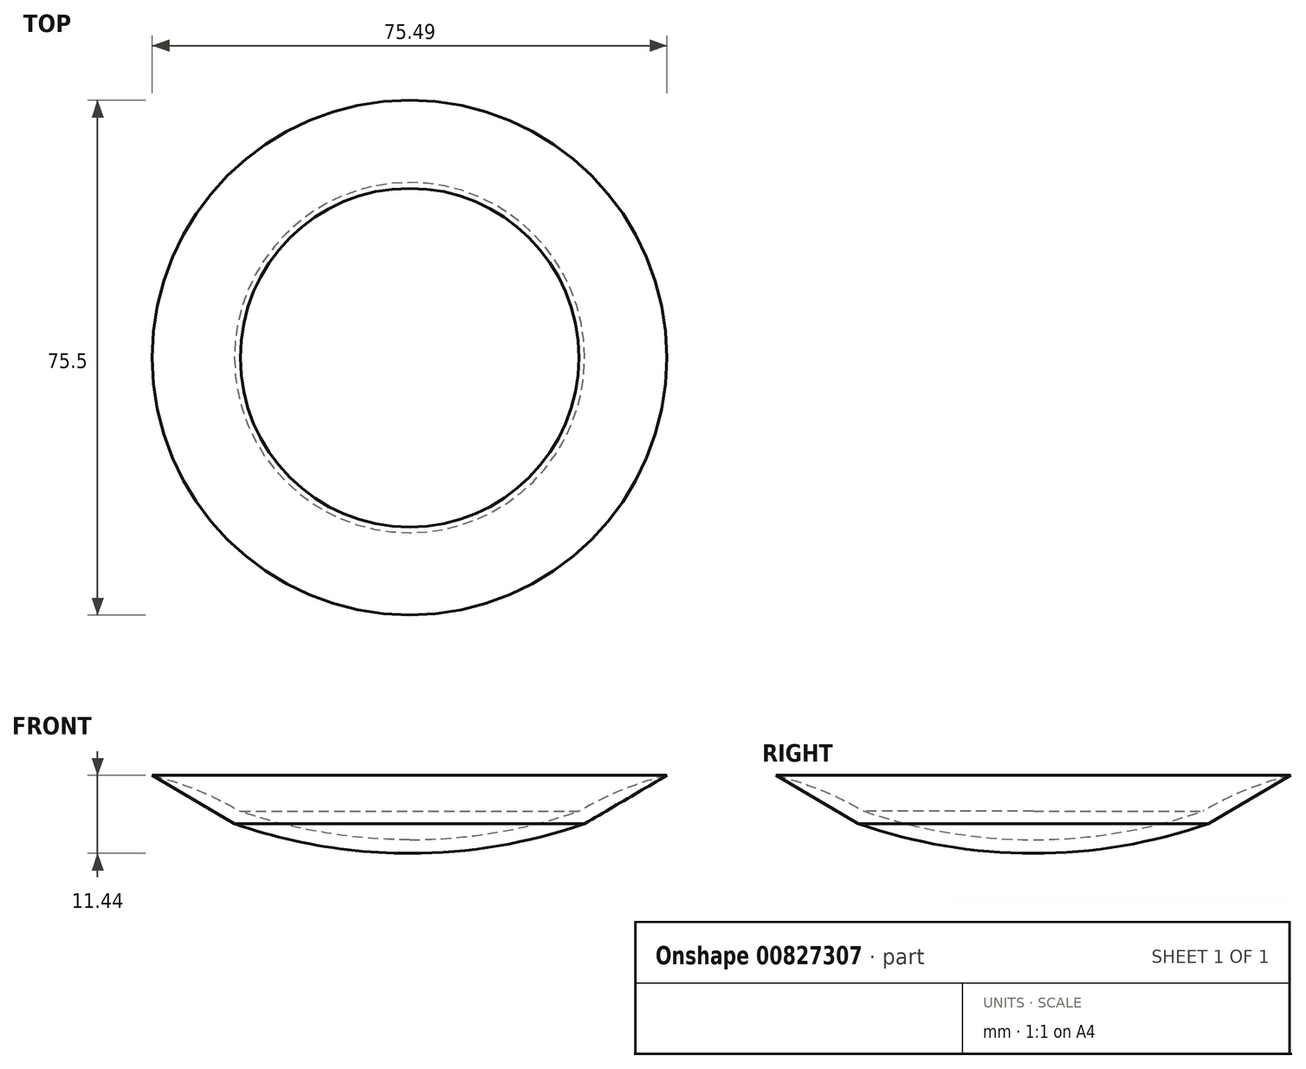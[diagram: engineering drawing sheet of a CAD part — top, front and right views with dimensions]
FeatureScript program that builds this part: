
annotation { "Feature Type Name" : "Feature", "Feature Type Description" : "" }
export const myFeature = defineFeature(function(context is Context, id is Id, definition is map)
    precondition{}
    {
        {
            var Q0;
            Q0=qCreatedBy(makeId("Front.planeOp"),FACE);
            var sketch = newSketch(context, id + "F0", { "sketchPlane" : qUnion([Q0])});
            skArc(sketch, "E0", {"start": v(-15.24, 15.43) * mm, "mid": v(-3, 12.3) * mm, "end": v(9.6, 11.26) * mm});
            skArc(sketch, "E1.0", {"start": v(-16.08, 13.6) * mm, "mid": v(-3.43, 10.35) * mm, "end": v(9.6, 9.26) * mm});
            skLineSegment(sketch, "E2", {"start": v(-16.08, 13.6) * mm, "end": v(-28.15, 20.7) * mm});
            skLineSegment(sketch, "E3", {"start": v(9.6, 11.26) * mm, "end": v(9.6, 9.26) * mm});
            skArc(sketch, "E4.trimOffspring", {"start": v(-15.24, 15.43) * mm, "mid": v(-21.51, 18.52) * mm, "end": v(-28.15, 20.7) * mm});
            skSolve(sketch);
        }
        {
            var Q0;
            Q0 = qSketchRegion(id + "F0", true);
            var Q1;
            Q1=sQuery(id+"F0.wireOp",EDGE,"E3");
            revolve(context, id + "F1", {"surfaceOperationType" : NewSurfaceOperationType.NEW, "entities" : qUnion([Q0]), "axis" : qUnion([Q1]), "revolveType" : RevolveType.FULL});
        }
    });
